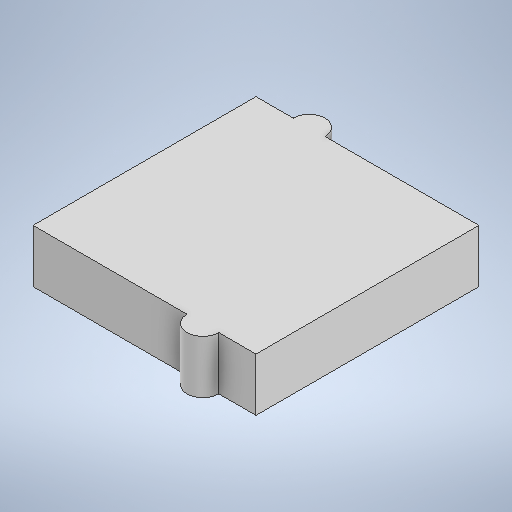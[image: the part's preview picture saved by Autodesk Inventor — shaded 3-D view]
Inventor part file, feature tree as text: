
AUTODESK INVENTOR PART (.ipt)
format: ipt  version: 2025.1 (Build 291241000, 241)  size: 224,768 bytes
history: native  units: mm
features: extrude x2, sketch x2
ambient origin geometry x8: Origin, YZ Plane, XZ Plane, XY Plane, X Axis, Y Axis, Z Axis, Center Point
bodies: Volumenkörper1 (feature_tree)
feature tree (4):
  extrude  "Extrusion1"  Depth=21.0mm
  extrude  "Extrusion2"  Depth=5.0mm
  sketch  "Skizze1"  dims[d0=21.0mm d1=21.0mm]
  sketch  "Skizze2"  dims[d2=5.0mm d3=0.0mm d4=3.0mm d5=3.0mm d6=5.5mm d7=5.5mm d8=5.0mm d9=0.0mm]
